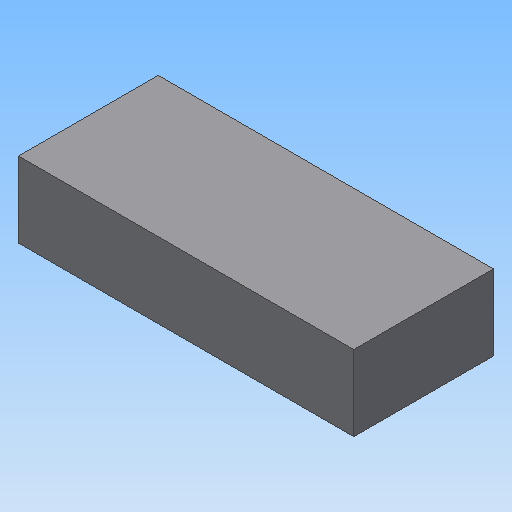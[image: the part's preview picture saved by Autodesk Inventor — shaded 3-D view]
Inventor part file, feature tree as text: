
AUTODESK INVENTOR PART (.ipt)
format: ipt  version: 2017 (Build 210142000, 142)  size: 77,312 bytes
history: native  units: in
note: dims shown in document units (in); Inventor stores cm internally (conversion verified against a paired STEP export)
features: extrude x1, sketch x1
ambient origin geometry x8: Origin, YZ Plane, XZ Plane, XY Plane, X Axis, Y Axis, Z Axis, Center Point
bodies: Solid1 (feature_tree)
feature tree (2):
  extrude  "Extrusion1"  Depth=1.063in
  sketch  "Sketch1"  dims[d0=4.7244in d1=1.063in d2=1.9685in d3=0.0in]
